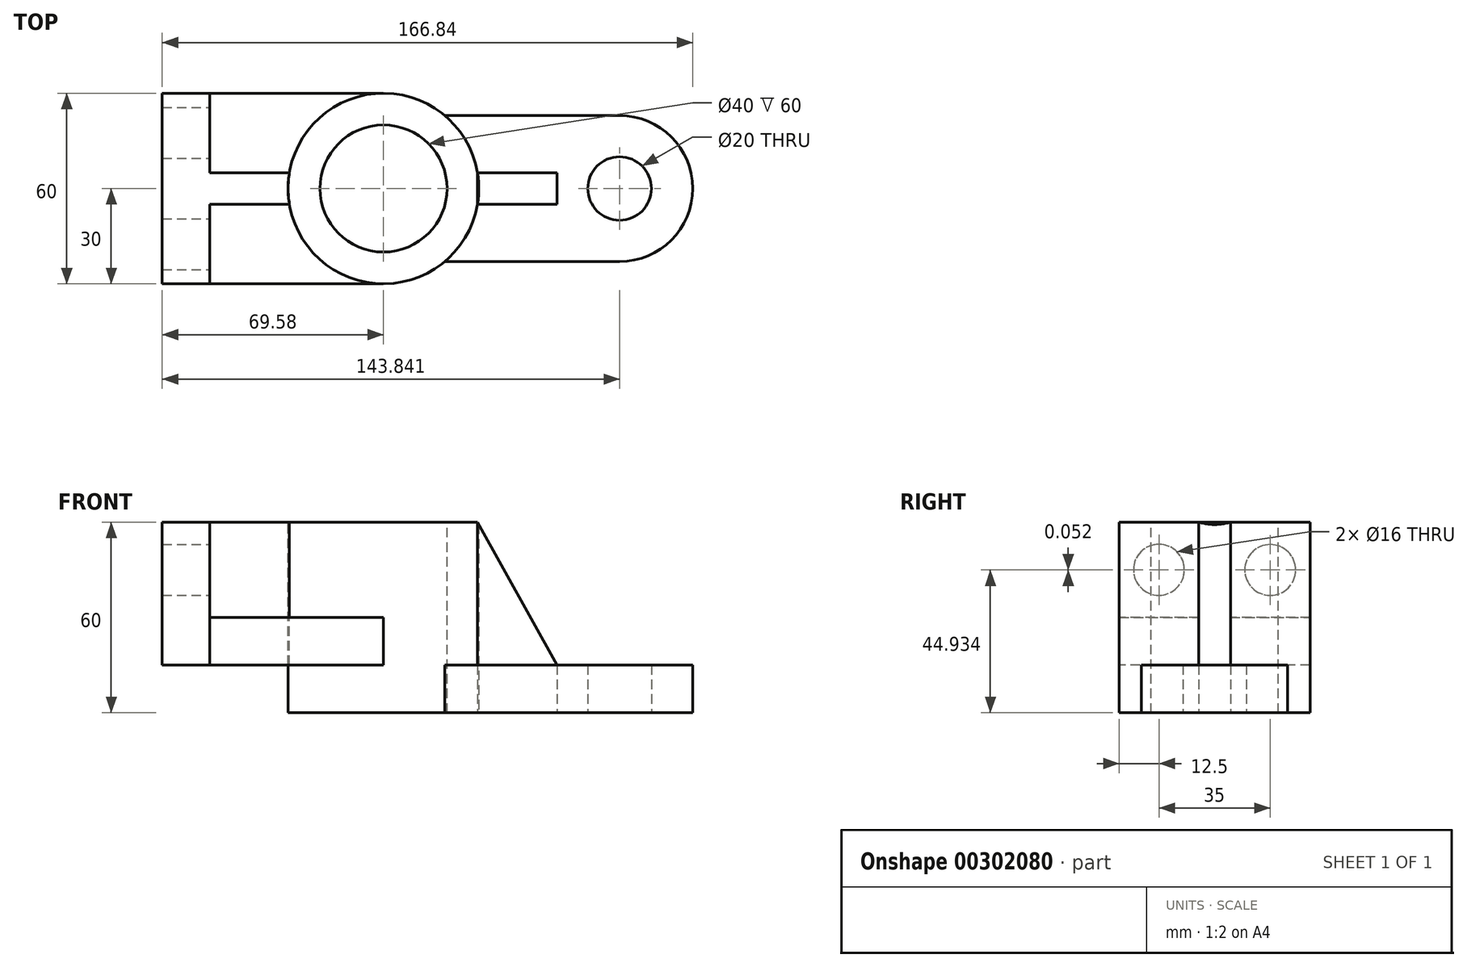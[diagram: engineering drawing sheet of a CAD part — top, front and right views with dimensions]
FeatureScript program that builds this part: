
annotation { "Feature Type Name" : "Feature", "Feature Type Description" : "" }
export const myFeature = defineFeature(function(context is Context, id is Id, definition is map)
    precondition{}
    {
        {
            var Q0;
            Q0=qCreatedBy(makeId("Top.planeOp"),FACE);
            var sketch = newSketch(context, id + "F0", { "sketchPlane" : qUnion([Q0])});
            skCircle(sketch, "E0", {"center": v(0, 0) * mm, "radius": 30 * mm});
            skCircle(sketch, "E1", {"center": v(0, 0) * mm, "radius": 20 * mm});
            skLineSegment(sketch, "E2", {"start": v(0, 30) * mm, "end": v(0, -30) * mm, "construction": true});
            skLineSegment(sketch, "E3", {"start": v(-30, 0) * mm, "end": v(30, 0) * mm, "construction": true});
            skLineSegment(sketch, "E4", {"start": v(-29.58, 5) * mm, "end": v(-54.58, 5) * mm});
            skLineSegment(sketch, "E5", {"start": v(-29.58, -5) * mm, "end": v(-54.58, -5) * mm});
            skLineSegment(sketch, "E6", {"start": v(-54.58, -30) * mm, "end": v(-54.58, -5) * mm});
            skLineSegment(sketch, "E7", {"start": v(-54.58, 30) * mm, "end": v(-69.58, 30) * mm});
            skLineSegment(sketch, "E8", {"start": v(-69.58, 30) * mm, "end": v(-69.58, -30) * mm});
            skLineSegment(sketch, "E9", {"start": v(-69.58, -30) * mm, "end": v(-54.58, -30) * mm});
            skLineSegment(sketch, "E10.trimOffspring", {"start": v(-54.58, 5) * mm, "end": v(-54.58, 30) * mm});
            skLineSegment(sketch, "E11", {"start": v(-54.58, 30) * mm, "end": v(0, 30) * mm});
            skLineSegment(sketch, "E12", {"start": v(-54.58, -30) * mm, "end": v(0, -30) * mm});
            skSolve(sketch);
        }
        {
            var Q0;
            Q0=makeQuery(id+"F0.imprint","IMPRINT",FACE,{"disambiguationData":[TD([[makeQuery(id+"F0.imprint","IMPRINT",EDGE,{"derivedFrom":sQuery(id+"F0.wireOp",EDGE,"E1")}),-1.0]])]});
            extrude(context, id + "F1", {"entities" : qUnion([Q0]), "oppositeDirection" : true, "depth" : 60 * mm});
        }
        {
            var Q0;
            Q0=makeQuery(id+"F1.opExtrude","CAP_FACE",FACE,{"disambiguationData":[OSD([sQuery(id+"F0.wireOp",EDGE,"E0"),sQuery(id+"F0.wireOp",EDGE,"E1")])],"isStart":true});
            var sketch = newSketch(context, id + "F2", { "sketchPlane" : qUnion([Q0])});
            skCircle(sketch, "E13.0", {"center": v(0, 0) * mm, "radius": 30 * mm});
            skCircle(sketch, "E13.1", {"center": v(0, 0) * mm, "radius": 20 * mm});
            skLineSegment(sketch, "E13.4", {"start": v(-29.58, 5) * mm, "end": v(-54.58, 5) * mm});
            skLineSegment(sketch, "E13.5", {"start": v(-29.58, -5) * mm, "end": v(-54.58, -5) * mm});
            skLineSegment(sketch, "E13.6", {"start": v(-54.58, -30) * mm, "end": v(-54.58, -5) * mm});
            skLineSegment(sketch, "E13.7", {"start": v(-54.58, 30) * mm, "end": v(-69.58, 30) * mm});
            skLineSegment(sketch, "E13.8", {"start": v(-69.58, 30) * mm, "end": v(-69.58, -30) * mm});
            skLineSegment(sketch, "E13.9", {"start": v(-69.58, -30) * mm, "end": v(-54.58, -30) * mm});
            skLineSegment(sketch, "E13.10", {"start": v(-54.58, 5) * mm, "end": v(-54.58, 30) * mm});
            skSolve(sketch);
        }
        {
            var Q0;
            {var subQ1=sQuery(id+"F2.wireOp",EDGE,"E13.4");Q0=makeQuery(id+"F2.imprint","IMPRINT",FACE,{"disambiguationData":[TD([[makeQuery(id+"F2.imprint","IMPRINT",EDGE,{"derivedFrom":subQ1}),1.0]])]});}
            extrude(context, id + "F3", {"entities" : qUnion([Q0]), "oppositeDirection" : true, "depth" : 45 * mm});
        }
        {
            var Q0;
            {var subQ0=sQuery(id+"F0.wireOp",EDGE,"E5");Q0=makeQuery(id+"F0.imprint","IMPRINT",FACE,{"disambiguationData":[TD([[makeQuery(id+"F0.imprint","IMPRINT",EDGE,{"derivedFrom":subQ0}),1.0]])]});}
            var Q1;
            {var subQ0=sQuery(id+"F0.wireOp",EDGE,"E4");Q1=makeQuery(id+"F0.imprint","IMPRINT",FACE,{"disambiguationData":[TD([[makeQuery(id+"F0.imprint","IMPRINT",EDGE,{"derivedFrom":subQ0}),-1.0]])]});}
            extrude(context, id + "F4", {"entities" : qUnion([Q0, Q1]), "oppositeDirection" : true, "depth" : 45 * mm});
        }
        {
            var Q0;
            Q0=makeQuery(id+"F4.opExtrude","CAP_FACE",FACE,{"disambiguationData":[OSD([sQuery(id+"F0.wireOp",EDGE,"E0"),sQuery(id+"F0.wireOp",EDGE,"E5"),sQuery(id+"F0.wireOp",EDGE,"E6"),sQuery(id+"F0.wireOp",EDGE,"E12")])],"isStart":true});
            var sketch = newSketch(context, id + "F5", { "sketchPlane" : qUnion([Q0])});
            skArc(sketch, "E14.0.0", {"start": v(0, -30) * mm, "mid": v(-19.36, -22.91) * mm, "end": v(-29.58, -5) * mm});
            skLineSegment(sketch, "E14.0.1", {"start": v(-29.58, -5) * mm, "end": v(-54.58, -5) * mm});
            skLineSegment(sketch, "E14.0.2", {"start": v(-54.58, -5) * mm, "end": v(-54.58, -30) * mm});
            skLineSegment(sketch, "E14.0.3", {"start": v(-54.58, -30) * mm, "end": v(0, -30) * mm});
            skArc(sketch, "E15.0.0", {"start": v(-29.58, 5) * mm, "mid": v(-19.36, 22.91) * mm, "end": v(0, 30) * mm});
            skLineSegment(sketch, "E15.0.1", {"start": v(0, 30) * mm, "end": v(-54.58, 30) * mm});
            skLineSegment(sketch, "E15.0.2", {"start": v(-54.58, 30) * mm, "end": v(-54.58, 5) * mm});
            skLineSegment(sketch, "E15.0.3", {"start": v(-54.58, 5) * mm, "end": v(-29.58, 5) * mm});
            skSolve(sketch);
        }
        {
            var Q0;
            Q0=makeQuery(id+"F5.imprint","IMPRINT",FACE,{"disambiguationData":[TD([[makeQuery(id+"F5.imprint","IMPRINT",EDGE,{"derivedFrom":sQuery(id+"F5.wireOp",EDGE,"E14.0.0")}),-1.0]])]});
            extrude(context, id + "F6", {"entities" : qUnion([Q0]), "operationType" : NewBodyOperationType.REMOVE, "oppositeDirection" : true, "depth" : 30 * mm});
        }
        {
            var Q0;
            Q0=makeQuery(id+"F4.opExtrude","CAP_FACE",FACE,{"disambiguationData":[OSD([sQuery(id+"F0.wireOp",EDGE,"E0"),sQuery(id+"F0.wireOp",EDGE,"E4"),sQuery(id+"F0.wireOp",EDGE,"E10.trimOffspring"),sQuery(id+"F0.wireOp",EDGE,"E11")])],"isStart":true});
            extrude(context, id + "F7", {"entities" : qUnion([Q0]), "operationType" : NewBodyOperationType.REMOVE, "oppositeDirection" : true, "depth" : 30 * mm});
        }
        {
            var Q0;
            Q0=makeQuery(id+"F3.opExtrude","SWEPT_FACE",FACE,{"disambiguationData":[OSD([sQuery(id+"F2.wireOp",EDGE,"E13.10")])]});
            var sketch = newSketch(context, id + "F8", { "sketchPlane" : qUnion([Q0])});
            skPoint(sketch, "E16.start.orphan", {"position": v(-30, -15.01) * mm});
            skLineSegment(sketch, "E17", {"start": v(-30, -15.01) * mm, "end": v(-5, -15.01) * mm, "construction": true});
            skLineSegment(sketch, "E18", {"start": v(30, -15.07) * mm, "end": v(5, -15.07) * mm, "construction": true});
            skPoint(sketch, "E18.endSnap0", {"position": v(5, -22.5) * mm});
            skCircle(sketch, "E19", {"center": v(-17.5, -15.01) * mm, "radius": 8 * mm});
            skCircle(sketch, "E20", {"center": v(17.5, -15.07) * mm, "radius": 8 * mm});
            skSolve(sketch);
        }
        {
            var Q0;
            Q0 = qSketchRegion(id + "F8", true);
            extrude(context, id + "F9", {"entities" : qUnion([Q0]), "operationType" : NewBodyOperationType.REMOVE, "endBound" : BoundingType.THROUGH_ALL, "oppositeDirection" : true, "depth" : 25 * mm});
        }
        {
            var Q0;
            Q0=makeQuery(id+"F1.opExtrude","CAP_FACE",FACE,{"disambiguationData":[OSD([sQuery(id+"F0.wireOp",EDGE,"E0"),sQuery(id+"F0.wireOp",EDGE,"E1")])],"isStart":false});
            var sketch = newSketch(context, id + "F10", { "sketchPlane" : qUnion([Q0])});
            skLineSegment(sketch, "E21", {"start": v(29.58, 5) * mm, "end": v(54.58, 5) * mm});
            skLineSegment(sketch, "E22", {"start": v(54.58, 5) * mm, "end": v(54.58, -5) * mm});
            skLineSegment(sketch, "E23", {"start": v(54.58, -5) * mm, "end": v(29.58, -5) * mm});
            skLineSegment(sketch, "E24", {"start": v(54.58, 0) * mm, "end": v(30, 0) * mm, "construction": true});
            skLineSegment(sketch, "E25", {"start": v(19.26, 23) * mm, "end": v(74.26, 23) * mm});
            skLineSegment(sketch, "E26", {"start": v(19.26, -23) * mm, "end": v(74.26, -23) * mm});
            skLineSegment(sketch, "E27", {"start": v(74.26, -23) * mm, "end": v(74.26, 23) * mm});
            skArc(sketch, "E28", {"start": v(74.26, -23) * mm, "mid": v(97.26, 0) * mm, "end": v(74.26, 23) * mm});
            skCircle(sketch, "E29", {"center": v(74.26, 0) * mm, "radius": 10 * mm});
            skSolve(sketch);
        }
        {
            var Q0;
            {var subQ1=sQuery(id+"F10.wireOp",EDGE,"E21");Q0=makeQuery(id+"F10.imprint","IMPRINT",FACE,{"disambiguationData":[TD([[makeQuery(id+"F10.imprint","IMPRINT",EDGE,{"derivedFrom":subQ1}),1.0]])]});}
            var Q1;
            {var subQ0=sQuery(id+"F10.wireOp",EDGE,"E28");Q1=makeQuery(id+"F10.imprint","IMPRINT",FACE,{"disambiguationData":[TD([[makeQuery(id+"F10.imprint","IMPRINT",EDGE,{"derivedFrom":subQ0}),1.0]])]});}
            extrude(context, id + "F11", {"entities" : qUnion([Q0, Q1]), "operationType" : NewBodyOperationType.ADD, "oppositeDirection" : true, "depth" : 15 * mm});
        }
        {
            var Q0;
            {var subQ0=sQuery(id+"F10.wireOp",EDGE,"E21");Q0=makeQuery(id+"F10.imprint","IMPRINT",FACE,{"disambiguationData":[TD([[makeQuery(id+"F10.imprint","IMPRINT",EDGE,{"derivedFrom":subQ0}),-1.0]])]});}
            extrude(context, id + "F12", {"entities" : qUnion([Q0]), "oppositeDirection" : true, "depth" : 60 * mm});
        }
        {
            var Q0;
            Q0=makeQuery(id+"F12.opExtrude","SWEPT_FACE",FACE,{"disambiguationData":[OSD([sQuery(id+"F10.wireOp",EDGE,"E21")])]});
            var sketch = newSketch(context, id + "F13", { "sketchPlane" : qUnion([Q0])});
            skPoint(sketch, "E30", {"position": v(54.58, -45) * mm});
            skLineSegment(sketch, "E31.0.0", {"start": v(29.58, -60) * mm, "end": v(54.58, -60) * mm});
            skLineSegment(sketch, "E31.0.1", {"start": v(54.58, -60) * mm, "end": v(54.58, 0) * mm});
            skLineSegment(sketch, "E31.0.2", {"start": v(54.58, 0) * mm, "end": v(29.58, 0) * mm});
            skLineSegment(sketch, "E31.0.3", {"start": v(29.58, 0) * mm, "end": v(29.58, -60) * mm});
            skLineSegment(sketch, "E32", {"start": v(54.58, -45) * mm, "end": v(29.58, 0) * mm});
            skLineSegment(sketch, "E33", {"start": v(29.58, 0) * mm, "end": v(54.58, 0) * mm});
            skLineSegment(sketch, "E34", {"start": v(54.58, -45) * mm, "end": v(54.58, 0) * mm});
            skSolve(sketch);
        }
        {
            var Q0;
            Q0=makeQuery(id+"F13.imprint","IMPRINT",FACE,{"disambiguationData":[TD([[makeQuery(id+"F13.imprint","IMPRINT",EDGE,{"derivedFrom":sQuery(id+"F13.wireOp",EDGE,"E32")}),-1.0]])]});
            extrude(context, id + "F14", {"entities" : qUnion([Q0]), "operationType" : NewBodyOperationType.REMOVE, "oppositeDirection" : true, "depth" : 10 * mm});
        }
    });
